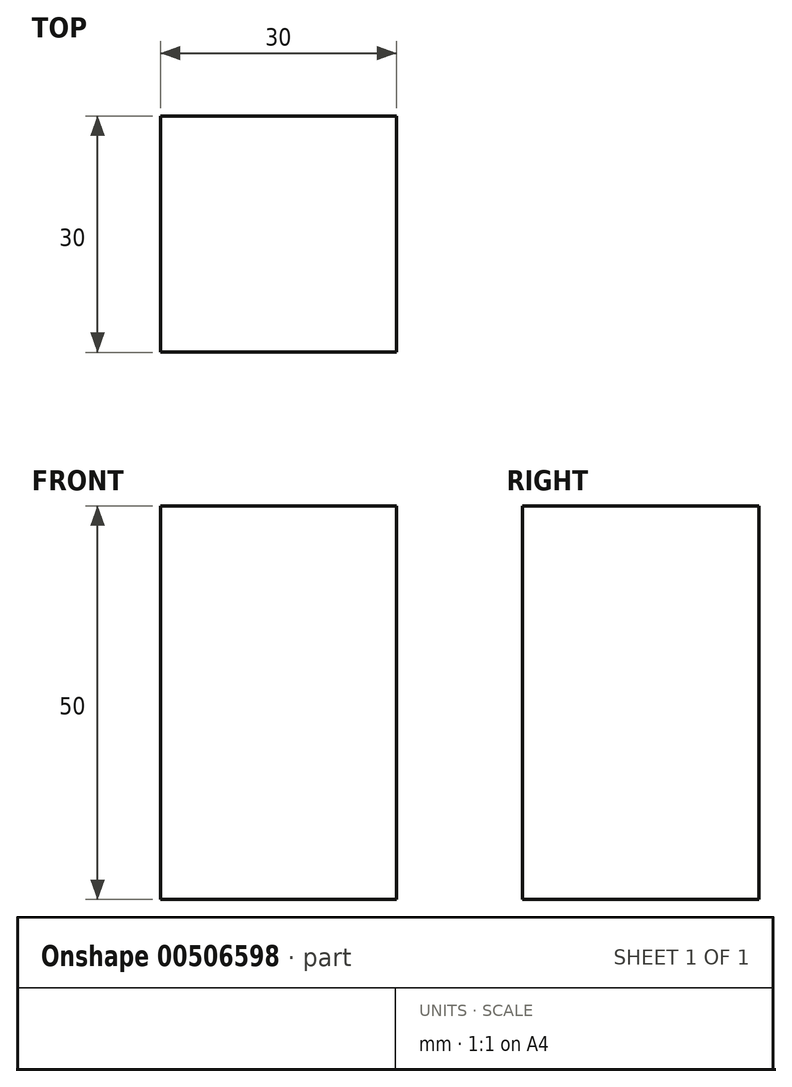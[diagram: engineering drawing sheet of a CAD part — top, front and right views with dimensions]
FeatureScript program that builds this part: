
annotation { "Feature Type Name" : "Feature", "Feature Type Description" : "" }
export const myFeature = defineFeature(function(context is Context, id is Id, definition is map)
    precondition{}
    {
        {
            var Q0;
            Q0=qCreatedBy(makeId("Top.planeOp"),FACE);
            var sketch = newSketch(context, id + "F0", { "sketchPlane" : qUnion([Q0])});
            skLineSegment(sketch, "E0.bottom", {"start": v(0, 6) * mm, "end": v(30, 6) * mm});
            skLineSegment(sketch, "E0.top", {"start": v(0, -24) * mm, "end": v(30, -24) * mm});
            skLineSegment(sketch, "E0.left", {"start": v(0, 6) * mm, "end": v(0, -24) * mm});
            skLineSegment(sketch, "E0.right", {"start": v(30, 6) * mm, "end": v(30, -24) * mm});
            skSolve(sketch);
        }
        {
            var Q0;
            Q0=makeQuery(id+"F0.imprint","IMPRINT",FACE,{"disambiguationData":[TD([[makeQuery(id+"F0.imprint","IMPRINT",EDGE,{"derivedFrom":sQuery(id+"F0.wireOp",EDGE,"E0.bottom")}),-1.0]])]});
            extrude(context, id + "F1", {"entities" : qUnion([Q0]), "depth" : 50 * mm, "offsetDistance" : 25 * mm});
        }
    });
